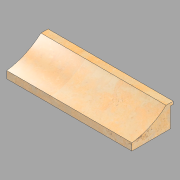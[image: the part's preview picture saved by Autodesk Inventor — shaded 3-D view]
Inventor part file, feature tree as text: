
AUTODESK INVENTOR PART (.ipt)
format: ipt  version: 2022.2 (Build 262287010, 287A)  size: 139,264 bytes
history: native  units: in
note: dims shown in document units (in); Inventor stores cm internally (conversion verified against a paired STEP export)
features: revolve x2, direct_edit x1, other x1
ambient origin geometry x8: Origin, YZ Plane, XZ Plane, XY Plane, X Axis, Y Axis, Z Axis, Center Point
bodies: Solid1 (feature_tree)
feature tree (4):
  direct_edit  "Direct Edit1"
  other  "Head (R) (1)"
  revolve  "Rotate1"  [1 undecoded]
  revolve  "Rotate2"  [1 undecoded]
note: 2 required parameter values undecoded (feature->parameter linkage not recoverable at this tier; creation-order binding heuristic only, values carry confidence <= 0.55)
